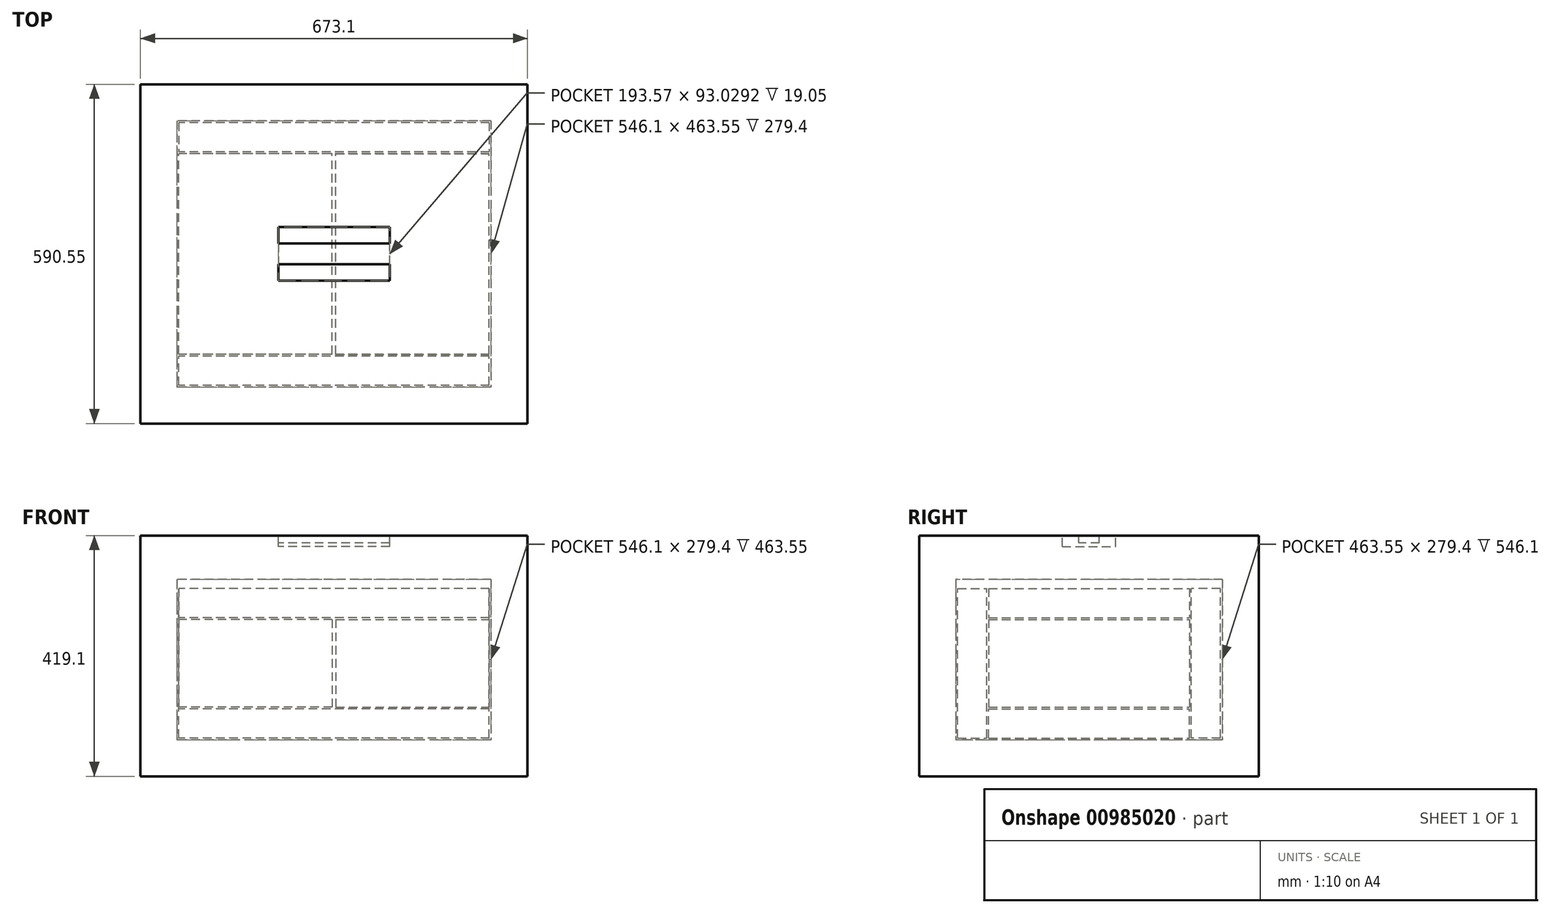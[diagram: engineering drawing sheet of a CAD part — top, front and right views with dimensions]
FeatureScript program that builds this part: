
annotation { "Feature Type Name" : "Feature", "Feature Type Description" : "" }
export const myFeature = defineFeature(function(context is Context, id is Id, definition is map)
    precondition{}
    {
        {
            var Q0;
            Q0=qCreatedBy(makeId("Top.planeOp"),FACE);
            var sketch = newSketch(context, id + "F0", { "sketchPlane" : qUnion([Q0])});
            skLineSegment(sketch, "E0.bottom", {"start": v(0, 0) * mm, "end": v(266.7, 0) * mm});
            skLineSegment(sketch, "E0.top", {"start": v(0, 349.25) * mm, "end": v(266.7, 349.25) * mm});
            skLineSegment(sketch, "E0.left", {"start": v(0, 0) * mm, "end": v(0, 349.25) * mm});
            skLineSegment(sketch, "E0.right", {"start": v(266.7, 0) * mm, "end": v(266.7, 349.25) * mm});
            skSolve(sketch);
        }
        {
            var Q0;
            Q0=makeQuery(id+"F0.imprint","IMPRINT",FACE,{"disambiguationData":[TD([[makeQuery(id+"F0.imprint","IMPRINT",EDGE,{"derivedFrom":sQuery(id+"F0.wireOp",EDGE,"E0.bottom")}),1.0]])]});
            extrude(context, id + "F1", {"entities" : qUnion([Q0]), "depth" : 152.4 * mm, "offsetDistance" : 25.4 * mm});
        }
        {
            var Q0;
            Q0=makeQuery(id+"F1.opExtrude","SWEPT_BODY",BODY,{"disambiguationData":[OSD([sQuery(id+"F0.wireOp",EDGE,"E0.bottom"),sQuery(id+"F0.wireOp",EDGE,"E0.top"),sQuery(id+"F0.wireOp",EDGE,"E0.left"),sQuery(id+"F0.wireOp",EDGE,"E0.right")])]});
            var Q1;
            Q1=makeQuery(id+"F1.opExtrude","CAP_EDGE",EDGE,{"disambiguationData":[OSD([sQuery(id+"F0.wireOp",EDGE,"E0.bottom")])],"isStart":true});
            var Q2;
            Q2=makeQuery(id+"F1.opExtrude","CAP_EDGE",EDGE,{"disambiguationData":[OSD([sQuery(id+"F0.wireOp",EDGE,"E0.bottom")])],"isStart":true});
            transform(context, id + "F2", {"entities" : qUnion([Q0]), "transformType" : TransformType.TRANSLATION_DISTANCE, "transformDirection" : qUnion([Q2]), "distance" : 3.17 * mm, "makeCopy" : false});
        }
        {
            var Q0;
            Q0=makeQuery(id+"F1.opExtrude","SWEPT_BODY",BODY,{"disambiguationData":[OSD([sQuery(id+"F0.wireOp",EDGE,"E0.bottom"),sQuery(id+"F0.wireOp",EDGE,"E0.top"),sQuery(id+"F0.wireOp",EDGE,"E0.left"),sQuery(id+"F0.wireOp",EDGE,"E0.right")])]});
            var Q1;
            Q1=qCreatedBy(makeId("Right.planeOp"),FACE);
            mirror(context, id + "F3", {"entities" : qUnion([Q0]), "mirrorPlane" : qUnion([Q1])});
        }
        {
            var Q0;
            Q0=makeQuery(id+"F1.opExtrude","CAP_FACE",FACE,{"disambiguationData":[OSD([sQuery(id+"F0.wireOp",EDGE,"E0.bottom"),sQuery(id+"F0.wireOp",EDGE,"E0.top"),sQuery(id+"F0.wireOp",EDGE,"E0.left"),sQuery(id+"F0.wireOp",EDGE,"E0.right")])],"isStart":false});
            cPlane(context, id + "F4", {"entities" : qUnion([Q0]), "cplaneType" : CPlaneType.OFFSET, "offset" : 3.17 * mm, "width" : 152.4 * mm, "height" : 152.4 * mm});
        }
        {
            var Q0;
            Q0=qCreatedBy(id+"F4.planeOp",FACE);
            var sketch = newSketch(context, id + "F5", { "sketchPlane" : qUnion([Q0])});
            skPoint(sketch, "E1.0", {"position": v(269.88, 0) * mm});
            skPoint(sketch, "E2.0", {"position": v(269.88, 349.25) * mm});
            skPoint(sketch, "E3.0", {"position": v(-269.88, 349.25) * mm});
            skPoint(sketch, "E4.0", {"position": v(-269.88, 0) * mm});
            skLineSegment(sketch, "E5.bottom", {"start": v(269.88, 0) * mm, "end": v(-269.88, 0) * mm});
            skLineSegment(sketch, "E5.top", {"start": v(269.88, 349.25) * mm, "end": v(-269.88, 349.25) * mm});
            skLineSegment(sketch, "E5.left", {"start": v(269.88, 0) * mm, "end": v(269.88, 349.25) * mm});
            skLineSegment(sketch, "E5.right", {"start": v(-269.88, 0) * mm, "end": v(-269.88, 349.25) * mm});
            skSolve(sketch);
        }
        {
            var Q0;
            Q0=makeQuery(id+"F5.imprint","IMPRINT",FACE,{"disambiguationData":[TD([[makeQuery(id+"F5.imprint","IMPRINT",EDGE,{"derivedFrom":sQuery(id+"F5.wireOp",EDGE,"E5.bottom")}),-1.0]])]});
            extrude(context, id + "F6", {"entities" : qUnion([Q0]), "depth" : 50.8 * mm, "offsetDistance" : 25.4 * mm});
        }
        {
            var Q0;
            Q0=makeQuery(id+"F1.opExtrude","SWEPT_EDGE",EDGE,{"disambiguationData":[OSD([sQuery(id+"F0.wireOp",EDGE,"E0.top"),sQuery(id+"F0.wireOp",EDGE,"E0.right")])]});
            cPoint(context, id + "F7", {"entities" : qUnion([Q0]), "parameter" : 0.5});
        }
        {
            var Q0;
            Q0=makeQuery(id+"F1.opExtrude","SWEPT_EDGE",EDGE,{"disambiguationData":[OSD([sQuery(id+"F0.wireOp",EDGE,"E0.top"),sQuery(id+"F0.wireOp",EDGE,"E0.left")])]});
            cPoint(context, id + "F8", {"entities" : qUnion([Q0]), "parameter" : 0.5});
        }
        {
            var Q0;
            Q0=makeQuery(id+"F1.opExtrude","SWEPT_EDGE",EDGE,{"disambiguationData":[OSD([sQuery(id+"F0.wireOp",EDGE,"E0.bottom"),sQuery(id+"F0.wireOp",EDGE,"E0.right")])]});
            cPoint(context, id + "F9", {"entities" : qUnion([Q0]), "parameter" : 0.5});
        }
        {
            var Q0;
            Q0 = qCreatedBy(id + "F7" ,VERTEX);
            var Q1;
            Q1 = qCreatedBy(id + "F8" ,VERTEX);
            var Q2;
            Q2 = qCreatedBy(id + "F9" ,VERTEX);
            cPlane(context, id + "F10", {"entities" : qUnion([Q0, Q1, Q2]), "cplaneType" : CPlaneType.THREE_POINT, "offset" : 25.4 * mm, "width" : 152.4 * mm, "height" : 152.4 * mm});
        }
        {
            var Q0;
            Q0=makeQuery(id+"F6.opExtrude","SWEPT_BODY",BODY,{"disambiguationData":[OSD([sQuery(id+"F5.wireOp",EDGE,"E5.bottom"),sQuery(id+"F5.wireOp",EDGE,"E5.top"),sQuery(id+"F5.wireOp",EDGE,"E5.left"),sQuery(id+"F5.wireOp",EDGE,"E5.right")])]});
            var Q1;
            Q1=qCreatedBy(id+"F10.planeOp",FACE);
            mirror(context, id + "F11", {"entities" : qUnion([Q0]), "mirrorPlane" : qUnion([Q1])});
        }
        {
            var Q0;
            Q0=qCreatedBy(makeId("Front.planeOp"),FACE);
            cPlane(context, id + "F12", {"entities" : qUnion([Q0]), "cplaneType" : CPlaneType.OFFSET, "offset" : 3.17 * mm, "width" : 152.4 * mm, "height" : 152.4 * mm});
        }
        {
            var Q0;
            Q0=qCreatedBy(id+"F12.planeOp",FACE);
            var sketch = newSketch(context, id + "F13", { "sketchPlane" : qUnion([Q0])});
            skPoint(sketch, "E6.0", {"position": v(269.88, -53.97) * mm});
            skPoint(sketch, "E7.0", {"position": v(-269.88, 206.38) * mm});
            skLineSegment(sketch, "E8.bottom", {"start": v(269.88, -53.97) * mm, "end": v(-269.87, -53.98) * mm});
            skLineSegment(sketch, "E8.top", {"start": v(269.88, 206.38) * mm, "end": v(-269.88, 206.38) * mm});
            skLineSegment(sketch, "E8.left", {"start": v(269.88, -53.97) * mm, "end": v(269.88, 206.38) * mm});
            skLineSegment(sketch, "E8.right", {"start": v(-269.87, -53.98) * mm, "end": v(-269.88, 206.38) * mm});
            skSolve(sketch);
        }
        {
            var Q0;
            Q0=makeQuery(id+"F13.imprint","IMPRINT",FACE,{"disambiguationData":[TD([[makeQuery(id+"F13.imprint","IMPRINT",EDGE,{"derivedFrom":sQuery(id+"F13.wireOp",EDGE,"E8.bottom")}),-1.0]])]});
            extrude(context, id + "F14", {"entities" : qUnion([Q0]), "depth" : 50.8 * mm, "offsetDistance" : 25.4 * mm});
        }
        {
            var Q0;
            Q0=makeQuery(id+"F1.opExtrude","CAP_EDGE",EDGE,{"disambiguationData":[OSD([sQuery(id+"F0.wireOp",EDGE,"E0.right")])],"isStart":true});
            cPoint(context, id + "F15", {"entities" : qUnion([Q0]), "parameter" : 0.5});
        }
        {
            var Q0;
            Q0=makeQuery(id+"F1.opExtrude","CAP_EDGE",EDGE,{"disambiguationData":[OSD([sQuery(id+"F0.wireOp",EDGE,"E0.right")])],"isStart":false});
            cPoint(context, id + "F16", {"entities" : qUnion([Q0]), "parameter" : 0.5});
        }
        {
            var Q0;
            Q0=makeQuery(id+"F3.opPattern","COPY",EDGE,{"derivedFrom":makeQuery(id+"F1.opExtrude","CAP_EDGE",EDGE,{"disambiguationData":[OSD([sQuery(id+"F0.wireOp",EDGE,"E0.right")])],"isStart":false}),"instanceName":"1"});
            cPoint(context, id + "F17", {"entities" : qUnion([Q0]), "parameter" : 0.5});
        }
        {
            var Q0;
            Q0 = qCreatedBy(id + "F15" ,VERTEX);
            var Q1;
            Q1 = qCreatedBy(id + "F16" ,VERTEX);
            var Q2;
            Q2 = qCreatedBy(id + "F17" ,VERTEX);
            cPlane(context, id + "F18", {"entities" : qUnion([Q0, Q1, Q2]), "cplaneType" : CPlaneType.THREE_POINT, "offset" : 25.4 * mm, "width" : 152.4 * mm, "height" : 152.4 * mm});
        }
        {
            var Q0;
            Q0=makeQuery(id+"F14.opExtrude","SWEPT_BODY",BODY,{"disambiguationData":[OSD([sQuery(id+"F13.wireOp",EDGE,"E8.bottom"),sQuery(id+"F13.wireOp",EDGE,"E8.top"),sQuery(id+"F13.wireOp",EDGE,"E8.left"),sQuery(id+"F13.wireOp",EDGE,"E8.right")])]});
            var Q1;
            Q1=qCreatedBy(id+"F18.planeOp",FACE);
            mirror(context, id + "F19", {"entities" : qUnion([Q0]), "mirrorPlane" : qUnion([Q1])});
        }
        {
            var Q0;
            Q0=makeQuery(id+"F11.opPattern","COPY",FACE,{"derivedFrom":makeQuery(id+"F6.opExtrude","CAP_FACE",FACE,{"disambiguationData":[OSD([sQuery(id+"F5.wireOp",EDGE,"E5.bottom"),sQuery(id+"F5.wireOp",EDGE,"E5.top"),sQuery(id+"F5.wireOp",EDGE,"E5.left"),sQuery(id+"F5.wireOp",EDGE,"E5.right")])],"isStart":false}),"instanceName":"1"});
            cPlane(context, id + "F20", {"entities" : qUnion([Q0]), "cplaneType" : CPlaneType.OFFSET, "offset" : 66.67 * mm, "width" : 152.4 * mm, "height" : 152.4 * mm});
        }
        {
            var Q0;
            Q0=qCreatedBy(id+"F20.planeOp",FACE);
            var sketch = newSketch(context, id + "F21", { "sketchPlane" : qUnion([Q0])});
            skLineSegment(sketch, "E9.bottom", {"start": v(336.55, -469.9) * mm, "end": v(-336.55, -469.9) * mm});
            skLineSegment(sketch, "E9.top", {"start": v(336.55, 120.65) * mm, "end": v(-336.55, 120.65) * mm});
            skLineSegment(sketch, "E9.left", {"start": v(336.55, -469.9) * mm, "end": v(336.55, 120.65) * mm});
            skLineSegment(sketch, "E9.right", {"start": v(-336.55, -469.9) * mm, "end": v(-336.55, 120.65) * mm});
            skLineSegment(sketch, "E10.0", {"start": v(269.88, -403.23) * mm, "end": v(-269.87, -403.23) * mm});
            skLineSegment(sketch, "E11.0", {"start": v(269.88, 53.98) * mm, "end": v(-269.88, 53.98) * mm});
            skSolve(sketch);
        }
        {
            var Q0;
            Q0=makeQuery(id+"F21.imprint","IMPRINT",FACE,{"disambiguationData":[TD([[makeQuery(id+"F21.imprint","IMPRINT",EDGE,{"derivedFrom":sQuery(id+"F21.wireOp",EDGE,"E9.bottom")}),-1.0]])]});
            extrude(context, id + "F22", {"entities" : qUnion([Q0]), "oppositeDirection" : true, "depth" : 368.3 * mm, "offsetDistance" : 25.4 * mm});
        }
        {
            var Q0;
            Q0=makeQuery(id+"F22.opExtrude","CAP_FACE",FACE,{"disambiguationData":[OSD([sQuery(id+"F21.wireOp",EDGE,"E9.bottom"),sQuery(id+"F21.wireOp",EDGE,"E9.top"),sQuery(id+"F21.wireOp",EDGE,"E9.left"),sQuery(id+"F21.wireOp",EDGE,"E9.right")])],"isStart":false});
            shell(context, id + "F23", {"entities" : qUnion([Q0]), "thickness" : 63.5 * mm});
        }
        {
            var Q0;
            Q0=makeQuery(id+"F22.opExtrude","CAP_FACE",FACE,{"disambiguationData":[OSD([sQuery(id+"F21.wireOp",EDGE,"E9.bottom"),sQuery(id+"F21.wireOp",EDGE,"E9.top"),sQuery(id+"F21.wireOp",EDGE,"E9.left"),sQuery(id+"F21.wireOp",EDGE,"E9.right")])],"isStart":false});
            var sketch = newSketch(context, id + "F24", { "sketchPlane" : qUnion([Q0])});
            skLineSegment(sketch, "E12.bottom", {"start": v(273.05, -57.15) * mm, "end": v(-273.05, -57.15) * mm});
            skLineSegment(sketch, "E12.top", {"start": v(273.05, 406.4) * mm, "end": v(-273.05, 406.4) * mm});
            skLineSegment(sketch, "E12.left", {"start": v(273.05, -57.15) * mm, "end": v(273.05, 406.4) * mm});
            skLineSegment(sketch, "E12.right", {"start": v(-273.05, -57.15) * mm, "end": v(-273.05, 406.4) * mm});
            skSolve(sketch);
        }
        {
            var Q0;
            Q0=makeQuery(id+"F24.imprint","IMPRINT",FACE,{"disambiguationData":[TD([[makeQuery(id+"F24.imprint","IMPRINT",EDGE,{"derivedFrom":sQuery(id+"F24.wireOp",EDGE,"E12.bottom")}),-1.0]])]});
            extrude(context, id + "F25", {"entities" : qUnion([Q0]), "oppositeDirection" : true, "depth" : 25.4 * mm, "offsetDistance" : 25.4 * mm});
        }
        {
            var Q0;
            Q0=makeQuery(id+"F22.opExtrude","CAP_FACE",FACE,{"disambiguationData":[OSD([sQuery(id+"F21.wireOp",EDGE,"E9.bottom"),sQuery(id+"F21.wireOp",EDGE,"E9.top"),sQuery(id+"F21.wireOp",EDGE,"E9.left"),sQuery(id+"F21.wireOp",EDGE,"E9.right")])],"isStart":false});
            var Q1;
            Q1=makeQuery(id+"F25.opExtrude","CAP_FACE",FACE,{"disambiguationData":[OSD([sQuery(id+"F24.wireOp",EDGE,"E12.bottom"),sQuery(id+"F24.wireOp",EDGE,"E12.top"),sQuery(id+"F24.wireOp",EDGE,"E12.left"),sQuery(id+"F24.wireOp",EDGE,"E12.right")])],"isStart":true});
            extrude(context, id + "F26", {"entities" : qUnion([Q0, Q1]), "operationType" : NewBodyOperationType.ADD, "depth" : 50.8 * mm, "offsetDistance" : 25.4 * mm});
        }
        {
            var Q0;
            Q0=makeQuery(id+"F26.boolean.opBoolean","MERGE",FACE,{"derivedFrom":[makeQuery(id+"F26.opExtrude","CAP_FACE",FACE,{"disambiguationData":[OSD([sQuery(id+"F21.wireOp",EDGE,"E9.bottom"),sQuery(id+"F21.wireOp",EDGE,"E9.top"),sQuery(id+"F21.wireOp",EDGE,"E9.left"),sQuery(id+"F21.wireOp",EDGE,"E9.right")])],"isStart":false}),makeQuery(id+"F26.opExtrude","CAP_FACE",FACE,{"disambiguationData":[OSD([sQuery(id+"F24.wireOp",EDGE,"E12.bottom"),sQuery(id+"F24.wireOp",EDGE,"E12.top"),sQuery(id+"F24.wireOp",EDGE,"E12.left"),sQuery(id+"F24.wireOp",EDGE,"E12.right")])],"isStart":false})]});
            var sketch = newSketch(context, id + "F27", { "sketchPlane" : qUnion([Q0])});
            skLineSegment(sketch, "E13.bottom", {"start": v(96.79, 128.11) * mm, "end": v(-96.79, 128.11) * mm});
            skLineSegment(sketch, "E13.top", {"start": v(96.79, 221.14) * mm, "end": v(-96.79, 221.14) * mm});
            skLineSegment(sketch, "E13.left", {"start": v(96.79, 128.11) * mm, "end": v(96.79, 221.14) * mm});
            skLineSegment(sketch, "E13.right", {"start": v(-96.79, 128.11) * mm, "end": v(-96.79, 221.14) * mm});
            skPoint(sketch, "E13.middle", {"position": v(0, 174.62) * mm});
            skPoint(sketch, "E13.middle.positionSnap0", {"position": v(336.55, 174.62) * mm});
            skPoint(sketch, "E13.centerSnap0", {"position": v(336.55, 174.62) * mm});
            skLineSegment(sketch, "E14.bottom", {"start": v(96.79, 156.63) * mm, "end": v(-96.79, 156.63) * mm});
            skLineSegment(sketch, "E14.top", {"start": v(96.79, 192.62) * mm, "end": v(-96.79, 192.62) * mm});
            skLineSegment(sketch, "E14.left", {"start": v(96.79, 156.63) * mm, "end": v(96.79, 192.62) * mm});
            skLineSegment(sketch, "E14.right", {"start": v(-96.79, 156.63) * mm, "end": v(-96.79, 192.62) * mm});
            skSolve(sketch);
        }
        {
            var Q0;
            {var subQ0=sQuery(id+"F27.wireOp",EDGE,"E13.bottom");Q0=makeQuery(id+"F27.imprint","IMPRINT",FACE,{"disambiguationData":[TD([[makeQuery(id+"F27.imprint","IMPRINT",EDGE,{"derivedFrom":subQ0}),-1.0]])]});}
            var Q1;
            Q1=makeQuery(id+"F27.imprint","IMPRINT",FACE,{"disambiguationData":[TD([[makeQuery(id+"F27.imprint","IMPRINT",EDGE,{"derivedFrom":sQuery(id+"F27.wireOp",EDGE,"E14.bottom")}),-1.0]])]});
            var Q2;
            {var subQ0=sQuery(id+"F27.wireOp",EDGE,"E13.top");Q2=makeQuery(id+"F27.imprint","IMPRINT",FACE,{"disambiguationData":[TD([[makeQuery(id+"F27.imprint","IMPRINT",EDGE,{"derivedFrom":subQ0}),1.0]])]});}
            extrude(context, id + "F28", {"entities" : qUnion([Q0, Q1, Q2]), "operationType" : NewBodyOperationType.REMOVE, "oppositeDirection" : true, "depth" : 19.05 * mm, "offsetDistance" : 25.4 * mm});
        }
        {
            var Q0;
            Q0=makeQuery(id+"F27.imprint","IMPRINT",FACE,{"disambiguationData":[TD([[makeQuery(id+"F27.imprint","IMPRINT",EDGE,{"derivedFrom":sQuery(id+"F27.wireOp",EDGE,"E14.bottom")}),-1.0]])]});
            var Q1;
            {var subQ6=sQuery(id+"F27.wireOp",EDGE,"E13.bottom");Q1=makeQuery(id+"F27.imprint","IMPRINT",FACE,{"disambiguationData":[TD([[makeQuery(id+"F27.imprint","IMPRINT",EDGE,{"derivedFrom":subQ6}),1.0]])]});}
            extrude(context, id + "F29", {"entities" : qUnion([Q0, Q1]), "operationType" : NewBodyOperationType.ADD, "oppositeDirection" : true, "depth" : 12.7 * mm, "offsetDistance" : 25.4 * mm});
        }
    });
